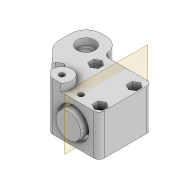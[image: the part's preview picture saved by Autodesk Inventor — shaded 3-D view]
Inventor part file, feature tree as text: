
AUTODESK INVENTOR PART (.ipt)
format: ipt  version: 2022 (Build 260153000, 153)  size: 384,000 bytes
history: native  units: mm
features: extrude x11, sketch x10, projected_geometry x8, fillet x3, plane x1, mirror x1
ambient origin geometry x8: Origin, YZ Plane, XZ Plane, XY Plane, X Axis, Y Axis, Z Axis, Center Point
bodies: Solid1 (feature_tree)
feature tree (34):
  extrude  "Extrusion1"  Depth=12.2mm
  extrude  "Extrusion2"  Depth=2.0mm
  extrude  "Extrusion3"  Depth=2.0mm TaperAngle=0.0deg
  plane  "Work Plane1"
  extrude  "Extrusion4"  Depth=3.0mm
  extrude  "Extrusion6"  Depth=7.0mm
  sketch  "Sketch6"  dims[d12=16.0mm d14=7.0mm]
  extrude  "Extrusion7"  Depth=6.0mm
  extrude  "Extrusion8"  Depth=4.1mm
  fillet  "Fillet1"  Radius=3.0mm
  fillet  "Fillet3"  Radius=4.1mm
  fillet  "Fillet4"  Radius=1.5mm
  extrude  "Extrusion9"  Depth=4.1mm
  extrude  "Extrusion10"  Depth=4.1mm
  extrude  "Extrusion11"  Depth=3.2mm TaperAngle=0.0deg
  extrude  "Extrusion12"  Depth=2.1mm
  mirror  "Mirror1"
  sketch  "Sketch1"  dims[d0=9.8mm d1=12.2mm]
  sketch  "Sketch2"  dims[d3=3.0mm d4=2.0mm]
  projected_geometry  "Projected Loop1"
  sketch  "Sketch3"  dims[d5=18.0mm d6=0.0mm d7=2.0mm d8=0.0mm]
  projected_geometry  "Projected Loop2"
  sketch  "Sketch5"  dims[d9=3.0mm d10=0.0mm d11=4.2mm]
  projected_geometry  "Projected Loop3"
  projected_geometry  "Projected Loop4"
  sketch  "Sketch8"  dims[d15=7.0mm d16=6.0mm]
  projected_geometry  "Projected Loop6"
  sketch  "Sketch9"  dims[d17=8.0mm d18=0.0mm d19=4.1mm d21=3.0mm d22=4.1mm d23=1.5mm]
  projected_geometry  "Projected Loop7"
  sketch  "Sketch10"  dims[d26=1.0mm d27=0.0mm d28=4.1mm]
  sketch  "Sketch11"  dims[d29=4.1mm d30=1.5mm]
  projected_geometry  "Projected Loop8"
  sketch  "Sketch12"  dims[d31=1.5mm d32=3.2mm d33=0.0mm d34=2.1mm d35=2.1mm d36=2.1mm d37=2.1mm d38=100.0mm d39=0.0mm d40=6.0mm d42=2.0mm d43=4.0mm d44=1.5mm d45=4.1mm d46=2.1mm d47=8.0mm d48=8.0mm d49=2.1mm d50=3.0mm d51=4.1mm d52=7.1mm d53=2.6mm d54=0.0mm d55=7.1mm d56=2.6mm d57=0.0mm d59=8.2mm d60=0.0mm d62=3.0mm d63=0.0mm d64=3.0mm d65=0.0mm d67=8.0mm]
  projected_geometry  "Projected Loop9"
